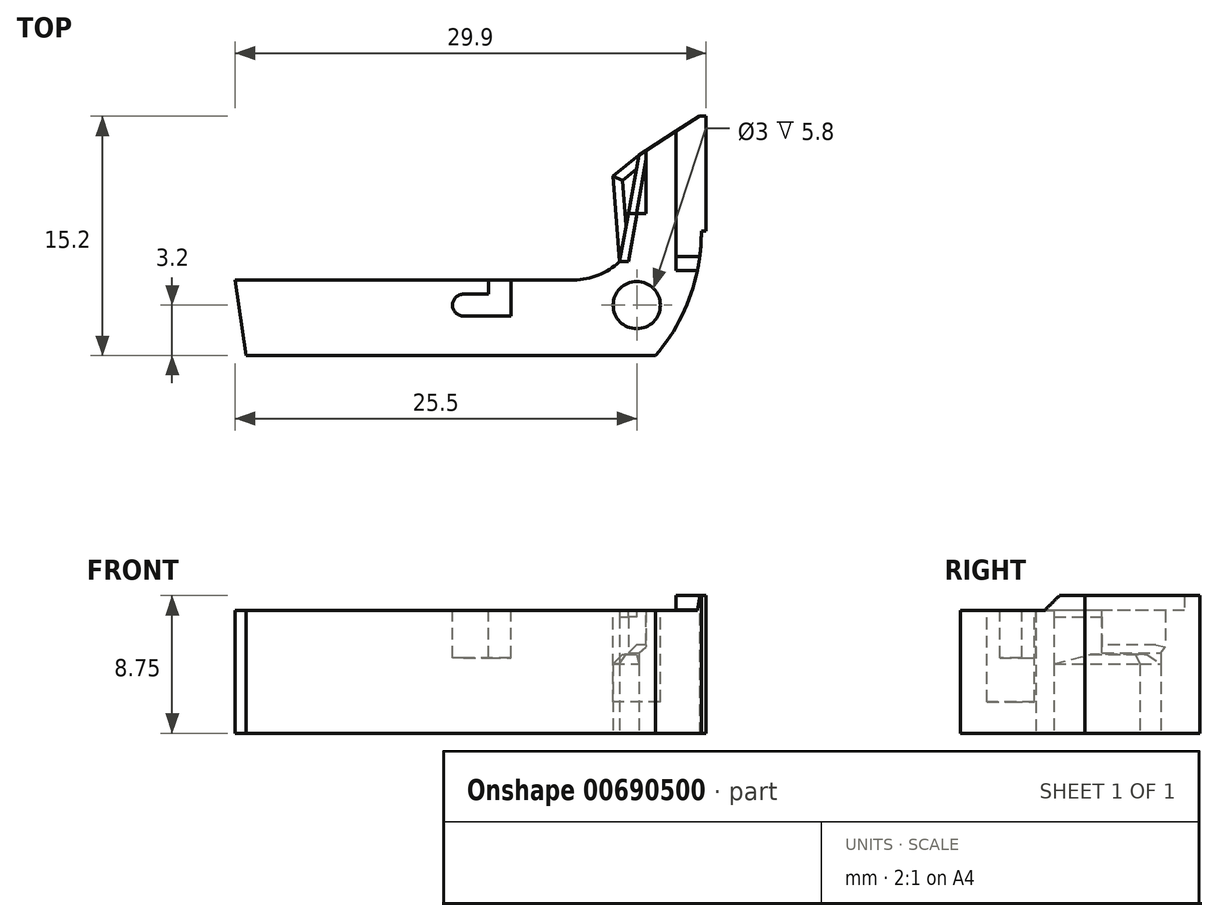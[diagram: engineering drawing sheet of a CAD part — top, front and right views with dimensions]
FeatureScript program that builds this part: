
annotation { "Feature Type Name" : "Feature", "Feature Type Description" : "" }
export const myFeature = defineFeature(function(context is Context, id is Id, definition is map)
    precondition{}
    {
        {
            var Q0;
            Q0=qCreatedBy(makeId("Top.planeOp"),FACE);
            var sketch = newSketch(context, id + "F0", { "sketchPlane" : qUnion([Q0])});
            skLineSegment(sketch, "E0", {"start": v(0, 0) * mm, "end": v(26, 0) * mm});
            skLineSegment(sketch, "E1", {"start": v(0, 0) * mm, "end": v(-0.7, 4.8) * mm});
            skLineSegment(sketch, "E2", {"start": v(-0.7, 4.8) * mm, "end": v(20.8, 4.8) * mm});
            skLineSegment(sketch, "E3", {"start": v(23.7, 5.96) * mm, "end": v(25.4, 15.2) * mm});
            skPoint(sketch, "E4.visualSharp", {"position": v(21.65, 5.06) * mm});
            skLineSegment(sketch, "E5", {"start": v(29.2, 7.9) * mm, "end": v(29.2, 15.2) * mm});
            skLineSegment(sketch, "E6", {"start": v(29.2, 7.9) * mm, "end": v(28.9, 7.9) * mm});
            skArc(sketch, "E7", {"start": v(26, 0) * mm, "mid": v(28.17, 3.69) * mm, "end": v(28.9, 7.9) * mm});
            skArc(sketch, "E8", {"start": v(20.8, 4.8) * mm, "mid": v(22.36, 5.1) * mm, "end": v(23.7, 5.96) * mm});
            skLineSegment(sketch, "E9", {"start": v(25.4, 15.2) * mm, "end": v(29.2, 15.2) * mm});
            skSolve(sketch);
        }
        {
            var Q0;
            Q0 = qSketchRegion(id + "F0", true);
            extrude(context, id + "F1", {"entities" : qUnion([Q0]), "depth" : 8.9 * mm, "offsetDistance" : 25 * mm});
        }
        {
            var Q0;
            Q0=makeQuery(id+"F1.opExtrude","CAP_FACE",FACE,{"disambiguationData":[OSD([sQuery(id+"F0.wireOp",EDGE,"E0"),sQuery(id+"F0.wireOp",EDGE,"E1"),sQuery(id+"F0.wireOp",EDGE,"E2"),sQuery(id+"F0.wireOp",EDGE,"E3"),sQuery(id+"F0.wireOp",EDGE,"E5"),sQuery(id+"F0.wireOp",EDGE,"E6"),sQuery(id+"F0.wireOp",EDGE,"E7"),sQuery(id+"F0.wireOp",EDGE,"E8"),sQuery(id+"F0.wireOp",EDGE,"E9")])],"isStart":false});
            var sketch = newSketch(context, id + "F2", { "sketchPlane" : qUnion([Q0])});
            skLineSegment(sketch, "E10.bottom", {"start": v(-0.7, 16.76) * mm, "end": v(27.3, 16.76) * mm});
            skLineSegment(sketch, "E10.top", {"start": v(-0.7, -8.07) * mm, "end": v(27.3, -8.07) * mm});
            skLineSegment(sketch, "E10.left", {"start": v(-0.7, 16.76) * mm, "end": v(-0.7, -8.07) * mm});
            skLineSegment(sketch, "E10.right", {"start": v(27.3, 16.76) * mm, "end": v(27.3, -8.07) * mm});
            skSolve(sketch);
        }
        {
            var Q0;
            Q0 = qSketchRegion(id + "F2", true);
            extrude(context, id + "F3", {"entities" : qUnion([Q0]), "operationType" : NewBodyOperationType.REMOVE, "oppositeDirection" : true, "depth" : 1.1 * mm, "offsetDistance" : 25 * mm});
        }
        {
            var Q0;
            Q0=makeQuery(id+"F1.opExtrude","CAP_FACE",FACE,{"disambiguationData":[OSD([sQuery(id+"F0.wireOp",EDGE,"E0"),sQuery(id+"F0.wireOp",EDGE,"E1"),sQuery(id+"F0.wireOp",EDGE,"E2"),sQuery(id+"F0.wireOp",EDGE,"E3"),sQuery(id+"F0.wireOp",EDGE,"E5"),sQuery(id+"F0.wireOp",EDGE,"E6"),sQuery(id+"F0.wireOp",EDGE,"E7"),sQuery(id+"F0.wireOp",EDGE,"E8"),sQuery(id+"F0.wireOp",EDGE,"E9")])],"isStart":false});
            var sketch = newSketch(context, id + "F4", { "sketchPlane" : qUnion([Q0])});
            skLineSegment(sketch, "E11.bottom", {"start": v(-14.25, 5.4) * mm, "end": v(67, 5.4) * mm});
            skLineSegment(sketch, "E11.top", {"start": v(-14.25, 0.4) * mm, "end": v(67, 0.4) * mm});
            skLineSegment(sketch, "E11.left", {"start": v(-14.25, 5.4) * mm, "end": v(-14.25, 0.4) * mm});
            skLineSegment(sketch, "E11.right", {"start": v(67, 5.4) * mm, "end": v(67, 0.4) * mm});
            skSolve(sketch);
        }
        {
            var Q0;
            Q0 = qSketchRegion(id + "F4", true);
            extrude(context, id + "F5", {"entities" : qUnion([Q0]), "operationType" : NewBodyOperationType.REMOVE, "oppositeDirection" : true, "depth" : 1.1 * mm, "offsetDistance" : 25 * mm});
        }
        {
            var Q0;
            Q0=makeQuery(id+"F5.boolean.opBoolean","MERGE",FACE,{"derivedFrom":[makeQuery(id+"F3.boolean.opBoolean","COPY",FACE,{"derivedFrom":makeQuery(id+"F3.opExtrude","CAP_FACE",FACE,{"disambiguationData":[OSD([sQuery(id+"F2.wireOp",EDGE,"E10.bottom"),sQuery(id+"F2.wireOp",EDGE,"E10.top"),sQuery(id+"F2.wireOp",EDGE,"E10.left"),sQuery(id+"F2.wireOp",EDGE,"E10.right")])],"isStart":false})}),makeQuery(id+"F5.opExtrude","CAP_FACE",FACE,{"disambiguationData":[OSD([sQuery(id+"F4.wireOp",EDGE,"E11.bottom"),sQuery(id+"F4.wireOp",EDGE,"E11.top"),sQuery(id+"F4.wireOp",EDGE,"E11.left"),sQuery(id+"F4.wireOp",EDGE,"E11.right")])],"isStart":false})]});
            var sketch = newSketch(context, id + "F6", { "sketchPlane" : qUnion([Q0])});
            skCircle(sketch, "E12", {"center": v(24.8, 3.2) * mm, "radius": 1.5 * mm});
            skSolve(sketch);
        }
        {
            var Q0;
            Q0 = qSketchRegion(id + "F6", true);
            extrude(context, id + "F7", {"entities" : qUnion([Q0]), "operationType" : NewBodyOperationType.REMOVE, "oppositeDirection" : true, "depth" : 5.8 * mm, "offsetDistance" : 25 * mm});
        }
        {
            var Q0;
            Q0=makeQuery(id+"F1.opExtrude","CAP_FACE",FACE,{"disambiguationData":[OSD([sQuery(id+"F0.wireOp",EDGE,"E0"),sQuery(id+"F0.wireOp",EDGE,"E1"),sQuery(id+"F0.wireOp",EDGE,"E2"),sQuery(id+"F0.wireOp",EDGE,"E3"),sQuery(id+"F0.wireOp",EDGE,"E5"),sQuery(id+"F0.wireOp",EDGE,"E6"),sQuery(id+"F0.wireOp",EDGE,"E7"),sQuery(id+"F0.wireOp",EDGE,"E8"),sQuery(id+"F0.wireOp",EDGE,"E9")])],"isStart":false});
            var sketch = newSketch(context, id + "F8", { "sketchPlane" : qUnion([Q0])});
            skLineSegment(sketch, "E13.bottom", {"start": v(24.53, 16.88) * mm, "end": v(33.22, 16.88) * mm});
            skLineSegment(sketch, "E13.top", {"start": v(24.53, 3.83) * mm, "end": v(33.22, 3.83) * mm});
            skLineSegment(sketch, "E13.left", {"start": v(24.53, 16.88) * mm, "end": v(24.53, 3.83) * mm});
            skLineSegment(sketch, "E13.right", {"start": v(33.22, 16.88) * mm, "end": v(33.22, 3.83) * mm});
            skSolve(sketch);
        }
        {
            var Q0;
            Q0 = qSketchRegion(id + "F8", true);
            extrude(context, id + "F9", {"entities" : qUnion([Q0]), "operationType" : NewBodyOperationType.REMOVE, "oppositeDirection" : true, "depth" : 0.15 * mm, "offsetDistance" : 25 * mm});
        }
        {
            var Q0;
            Q0=makeQuery(id+"F9.boolean.opBoolean","INTERSECT",EDGE,{"derivedFrom":[makeQuery(id+"F5.boolean.opBoolean","COPY",FACE,{"derivedFrom":makeQuery(id+"F5.opExtrude","SWEPT_FACE",FACE,{"disambiguationData":[OSD([sQuery(id+"F4.wireOp",EDGE,"E11.bottom")])]})}),makeQuery(id+"F9.opExtrude","CAP_FACE",FACE,{"disambiguationData":[OSD([sQuery(id+"F8.wireOp",EDGE,"E13.bottom"),sQuery(id+"F8.wireOp",EDGE,"E13.top"),sQuery(id+"F8.wireOp",EDGE,"E13.left"),sQuery(id+"F8.wireOp",EDGE,"E13.right")])],"isStart":false})]});
            chamfer(context, id + "F10", {"entities" : qUnion([Q0]), "width" : 0.9 * mm, "tangentPropagation" : true});
        }
        {
            var Q0;
            Q0=makeQuery(id+"F5.boolean.opBoolean","MERGE",FACE,{"derivedFrom":[makeQuery(id+"F3.boolean.opBoolean","COPY",FACE,{"derivedFrom":makeQuery(id+"F3.opExtrude","CAP_FACE",FACE,{"disambiguationData":[OSD([sQuery(id+"F2.wireOp",EDGE,"E10.bottom"),sQuery(id+"F2.wireOp",EDGE,"E10.top"),sQuery(id+"F2.wireOp",EDGE,"E10.left"),sQuery(id+"F2.wireOp",EDGE,"E10.right")])],"isStart":false})}),makeQuery(id+"F5.opExtrude","CAP_FACE",FACE,{"disambiguationData":[OSD([sQuery(id+"F4.wireOp",EDGE,"E11.bottom"),sQuery(id+"F4.wireOp",EDGE,"E11.top"),sQuery(id+"F4.wireOp",EDGE,"E11.left"),sQuery(id+"F4.wireOp",EDGE,"E11.right")])],"isStart":false})]});
            var sketch = newSketch(context, id + "F11", { "sketchPlane" : qUnion([Q0])});
            skCircle(sketch, "E14", {"center": v(13.8, 3.2) * mm, "radius": 0.7 * mm});
            skLineSegment(sketch, "E15", {"start": v(16.8, 2.5) * mm, "end": v(13.8, 2.5) * mm});
            skLineSegment(sketch, "E16", {"start": v(16.8, 2.5) * mm, "end": v(16.8, 4.8) * mm});
            skLineSegment(sketch, "E17", {"start": v(16.8, 4.8) * mm, "end": v(15.4, 4.8) * mm});
            skLineSegment(sketch, "E18", {"start": v(13.8, 3.9) * mm, "end": v(15.4, 3.9) * mm});
            skLineSegment(sketch, "E19", {"start": v(15.4, 3.9) * mm, "end": v(15.4, 4.8) * mm});
            skSolve(sketch);
        }
        {
            var Q0;
            Q0 = qSketchRegion(id + "F11", true);
            extrude(context, id + "F12", {"entities" : qUnion([Q0]), "operationType" : NewBodyOperationType.REMOVE, "oppositeDirection" : true, "depth" : 3 * mm, "offsetDistance" : 25 * mm});
        }
        {
            var Q0;
            Q0=makeQuery(id+"F5.boolean.opBoolean","MERGE",FACE,{"derivedFrom":[makeQuery(id+"F3.boolean.opBoolean","COPY",FACE,{"derivedFrom":makeQuery(id+"F3.opExtrude","CAP_FACE",FACE,{"disambiguationData":[OSD([sQuery(id+"F2.wireOp",EDGE,"E10.bottom"),sQuery(id+"F2.wireOp",EDGE,"E10.top"),sQuery(id+"F2.wireOp",EDGE,"E10.left"),sQuery(id+"F2.wireOp",EDGE,"E10.right")])],"isStart":false})}),makeQuery(id+"F5.opExtrude","CAP_FACE",FACE,{"disambiguationData":[OSD([sQuery(id+"F4.wireOp",EDGE,"E11.bottom"),sQuery(id+"F4.wireOp",EDGE,"E11.top"),sQuery(id+"F4.wireOp",EDGE,"E11.left"),sQuery(id+"F4.wireOp",EDGE,"E11.right")])],"isStart":false})]});
            var sketch = newSketch(context, id + "F13", { "sketchPlane" : qUnion([Q0])});
            skLineSegment(sketch, "E20.top", {"start": v(25.4, 9) * mm, "end": v(23.2, 9) * mm});
            skLineSegment(sketch, "E20.left", {"start": v(25.4, 15.2) * mm, "end": v(25.4, 9) * mm});
            skLineSegment(sketch, "E20.right", {"start": v(23.2, 15.2) * mm, "end": v(23.2, 9) * mm});
            skLineSegment(sketch, "E21", {"start": v(25.4, 15.2) * mm, "end": v(23.2, 15.2) * mm});
            skSolve(sketch);
        }
        {
            var Q0;
            Q0 = qSketchRegion(id + "F13", true);
            extrude(context, id + "F14", {"entities" : qUnion([Q0]), "operationType" : NewBodyOperationType.REMOVE, "oppositeDirection" : true, "depth" : 2.2 * mm, "offsetDistance" : 25 * mm});
        }
        {
            var Q0;
            Q0=makeQuery(id+"F14.boolean.opBoolean","INTERSECT",EDGE,{"derivedFrom":[makeQuery(id+"F1.opExtrude","SWEPT_FACE",FACE,{"disambiguationData":[OSD([sQuery(id+"F0.wireOp",EDGE,"E3")])]}),makeQuery(id+"F14.opExtrude","CAP_FACE",FACE,{"disambiguationData":[OSD([sQuery(id+"F13.wireOp",EDGE,"E20.bottom"),sQuery(id+"F13.wireOp",EDGE,"E20.top"),sQuery(id+"F13.wireOp",EDGE,"E20.left"),sQuery(id+"F13.wireOp",EDGE,"E20.right")])],"isStart":false})]});
            chamfer(context, id + "F15", {"entities" : qUnion([Q0]), "width" : 0.5 * mm, "tangentPropagation" : true});
        }
        {
            var Q0;
            Q0=makeQuery(id+"F5.boolean.opBoolean","MERGE",FACE,{"derivedFrom":[makeQuery(id+"F3.boolean.opBoolean","COPY",FACE,{"derivedFrom":makeQuery(id+"F3.opExtrude","CAP_FACE",FACE,{"disambiguationData":[OSD([sQuery(id+"F2.wireOp",EDGE,"E10.bottom"),sQuery(id+"F2.wireOp",EDGE,"E10.top"),sQuery(id+"F2.wireOp",EDGE,"E10.left"),sQuery(id+"F2.wireOp",EDGE,"E10.right")])],"isStart":false})}),makeQuery(id+"F5.opExtrude","CAP_FACE",FACE,{"disambiguationData":[OSD([sQuery(id+"F4.wireOp",EDGE,"E11.bottom"),sQuery(id+"F4.wireOp",EDGE,"E11.top"),sQuery(id+"F4.wireOp",EDGE,"E11.left"),sQuery(id+"F4.wireOp",EDGE,"E11.right")])],"isStart":false})]});
            var sketch = newSketch(context, id + "F16", { "sketchPlane" : qUnion([Q0])});
            skLineSegment(sketch, "E22", {"start": v(24.26, 9) * mm, "end": v(24.83, 9) * mm});
            skLineSegment(sketch, "E23", {"start": v(24.83, 9) * mm, "end": v(24.26, 5.96) * mm});
            skLineSegment(sketch, "E24", {"start": v(24.26, 5.96) * mm, "end": v(23.7, 5.96) * mm});
            skLineSegment(sketch, "E25", {"start": v(23.7, 5.96) * mm, "end": v(24.26, 9) * mm});
            skSolve(sketch);
        }
        {
            var Q0;
            Q0 = qSketchRegion(id + "F16", true);
            extrude(context, id + "F17", {"entities" : qUnion([Q0]), "operationType" : NewBodyOperationType.REMOVE, "oppositeDirection" : true, "depth" : 0.4 * mm, "offsetDistance" : 25 * mm});
        }
        {
            var Q0;
            Q0=makeQuery(id+"F1.opExtrude","CAP_FACE",FACE,{"disambiguationData":[OSD([sQuery(id+"F0.wireOp",EDGE,"E0"),sQuery(id+"F0.wireOp",EDGE,"E1"),sQuery(id+"F0.wireOp",EDGE,"E2"),sQuery(id+"F0.wireOp",EDGE,"E3"),sQuery(id+"F0.wireOp",EDGE,"E5"),sQuery(id+"F0.wireOp",EDGE,"E6"),sQuery(id+"F0.wireOp",EDGE,"E7"),sQuery(id+"F0.wireOp",EDGE,"E8"),sQuery(id+"F0.wireOp",EDGE,"E9")])],"isStart":true});
            var sketch = newSketch(context, id + "F18", { "sketchPlane" : qUnion([Q0])});
            skLineSegment(sketch, "E26", {"start": v(24.95, -12.74) * mm, "end": v(28.79, -15.2) * mm});
            skLineSegment(sketch, "E27", {"start": v(28.79, -15.2) * mm, "end": v(25.4, -15.2) * mm});
            skLineSegment(sketch, "E28", {"start": v(25.4, -15.2) * mm, "end": v(24.95, -12.74) * mm});
            skSolve(sketch);
        }
        {
            var Q0;
            Q0 = qSketchRegion(id + "F18", true);
            extrude(context, id + "F19", {"entities" : qUnion([Q0]), "operationType" : NewBodyOperationType.REMOVE, "oppositeDirection" : true, "depth" : 25 * mm, "offsetDistance" : 25 * mm});
        }
        {
            var Q0;
            Q0=makeQuery(id+"F1.opExtrude","CAP_FACE",FACE,{"disambiguationData":[OSD([sQuery(id+"F0.wireOp",EDGE,"E0"),sQuery(id+"F0.wireOp",EDGE,"E1"),sQuery(id+"F0.wireOp",EDGE,"E2"),sQuery(id+"F0.wireOp",EDGE,"E3"),sQuery(id+"F0.wireOp",EDGE,"E5"),sQuery(id+"F0.wireOp",EDGE,"E6"),sQuery(id+"F0.wireOp",EDGE,"E7"),sQuery(id+"F0.wireOp",EDGE,"E8"),sQuery(id+"F0.wireOp",EDGE,"E9")])],"isStart":true});
            var sketch = newSketch(context, id + "F20", { "sketchPlane" : qUnion([Q0])});
            skLineSegment(sketch, "E29", {"start": v(24.95, -12.74) * mm, "end": v(23.28, -11.4) * mm});
            skLineSegment(sketch, "E30", {"start": v(23.28, -11.4) * mm, "end": v(23.7, -5.96) * mm});
            skLineSegment(sketch, "E31", {"start": v(23.7, -5.96) * mm, "end": v(24.95, -12.74) * mm});
            skSolve(sketch);
        }
        {
            var Q0;
            Q0 = qSketchRegion(id + "F20", true);
            extrude(context, id + "F21", {"entities" : qUnion([Q0]), "operationType" : NewBodyOperationType.ADD, "oppositeDirection" : true, "depth" : 5 * mm, "offsetDistance" : 25 * mm});
        }
        {
            var Q0;
            Q0=makeQuery(id+"F21.opExtrude","CAP_EDGE",EDGE,{"disambiguationData":[OSD([sQuery(id+"F20.wireOp",EDGE,"E30")])],"isStart":false});
            var Q1;
            Q1=makeQuery(id+"F21.opExtrude","CAP_EDGE",EDGE,{"disambiguationData":[OSD([sQuery(id+"F20.wireOp",EDGE,"E29")])],"isStart":false});
            chamfer(context, id + "F22", {"entities" : qUnion([Q0, Q1]), "width" : 0.6 * mm, "tangentPropagation" : true});
        }
    });
